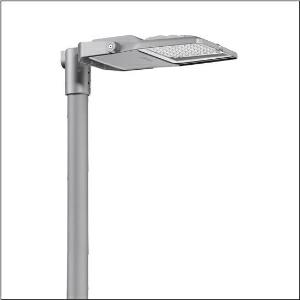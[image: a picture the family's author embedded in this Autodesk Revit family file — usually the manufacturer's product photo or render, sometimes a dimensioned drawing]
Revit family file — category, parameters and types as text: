
# Revit family: floodlight_fl_21_mini___pl52_5xa7775d2d3a_ca02
name_source: partatom
category: Lighting Fixtures
units: mm (PartAtom-declared; Revit-internal decimal feet)

## family parameters
Cut with Voids When Loaded = No
Host = Face
Light Source = No
Part Type = Normal
Room Calculation Point = No
Round Connector Dimension = Use Diameter
Shared = No

## types (1)
- --- (1 x LED, 17840 lm, 142.9 W, 3000K)
    Apparent Load = 143 VA
    CIE Flux Codes = 26 60 98 100 100
    Color Rendering = 70
    Color Temperature = 3000K
    Default Elevation = 1800 mm
    Description = Floodlight FL 21 mini, floodlight, primary light control with lens, of PMMA, primary optical cover: protective disc, of toughened safety glass, transparent, light distribution: PL52, light emission: direct distribution, installation type: surface-mounted, LED, High Power LED, rated luminous flux: 17.840lm, luminous efficacy: 125lm/W, light colour: 730, colour temperature: 3000K, control gear: Smart Interface (Zhaga), control: flexible luminous flux parameterisation, time-dependent luminous flux control, constant luminous flux control, overheat protection, pre-setting: logarithmic dimming characteristic, with terminal, 6-pole, mains connection: 220..240V, AC, 50/60Hz, start of lifetime: 143W, end of service life: 151W, reduction: 63W, luminaire housing, of diecast aluminium, powder-coated, SITECO metallic grey (DB 702S), corrosivity category C5 mid according to DIN EN ISO 12944, suitable for swimming pools, chlorine-resistant, sealing non-destructively replaceable, please order mast flange separately, mast bracket, of steel, galvanised, powder-coated, SITECO metallic grey (DB 702S), Smart Interface above, protection rating (complete): IP66, insulation class (complete): insulation class II (safety insulation), certification: CE, ENEC, VDE, protection symbol: D, impact resistance: IK08, permissible operating ambient temperature: -40..+40°C, permissible operating ambient temperature for outdoor applications: -40..+50°C, standard: DIN EN 12944, LABS conformity tested according to VDMA 24364:2018-05, packaging unit: 1 piece

Light Distribution: PL52
    Height = 70 mm
    Lamp = 1 x LED
    Lamp Light Flux = 17840 lm
    Lamp Power = 142.9 W
    Lamp count = 1
    Length = 485 mm
    Luminous efficacy = 125 lm/W
    Manufacturer = Siteco
    ModVariant = No
    Model = 5XA7775D2D3A
    Mounting Place = Pole
    Mounting Type = Pole annexe
    Number of Poles = 1
    OnlyDefault = Yes
    Power Factor = 1
    Product Name = Floodlight FL 21 mini | PL52
    Product group = floodlight | pylon annexe
    ProductGroupID = 6201
    Protection Class = Protection class II
    Protection Degree = IP 66
    RLX_Detail_Level = 1
    RLX_Emergency_Light_Flux = 0 lm
    RLX_Emergency_Type = 0
    RLX_Emergency_Type_DB = No
    RlxData = <blob elided: 101505 chars, md5=a54fdf50>
    Socket = socket
    Standby Power = 0 W
    System Light Flux = 17840 lm
    System Power = 143 W
    Type Comments = factory setting: luminous flux: 100 % | dim-lin: 254 | 730 mA
    Type Image = l_1007125.jpg
    URL = http://relux.com
    VarID = @adj_164203
    Voltage = 0 V
    Weight = 0.00 kg
    Width = 337 mm

## geometry (parser evidence)
native form markers: Blend x4, Sweep x11
no freeform markers — native parametric forms only
